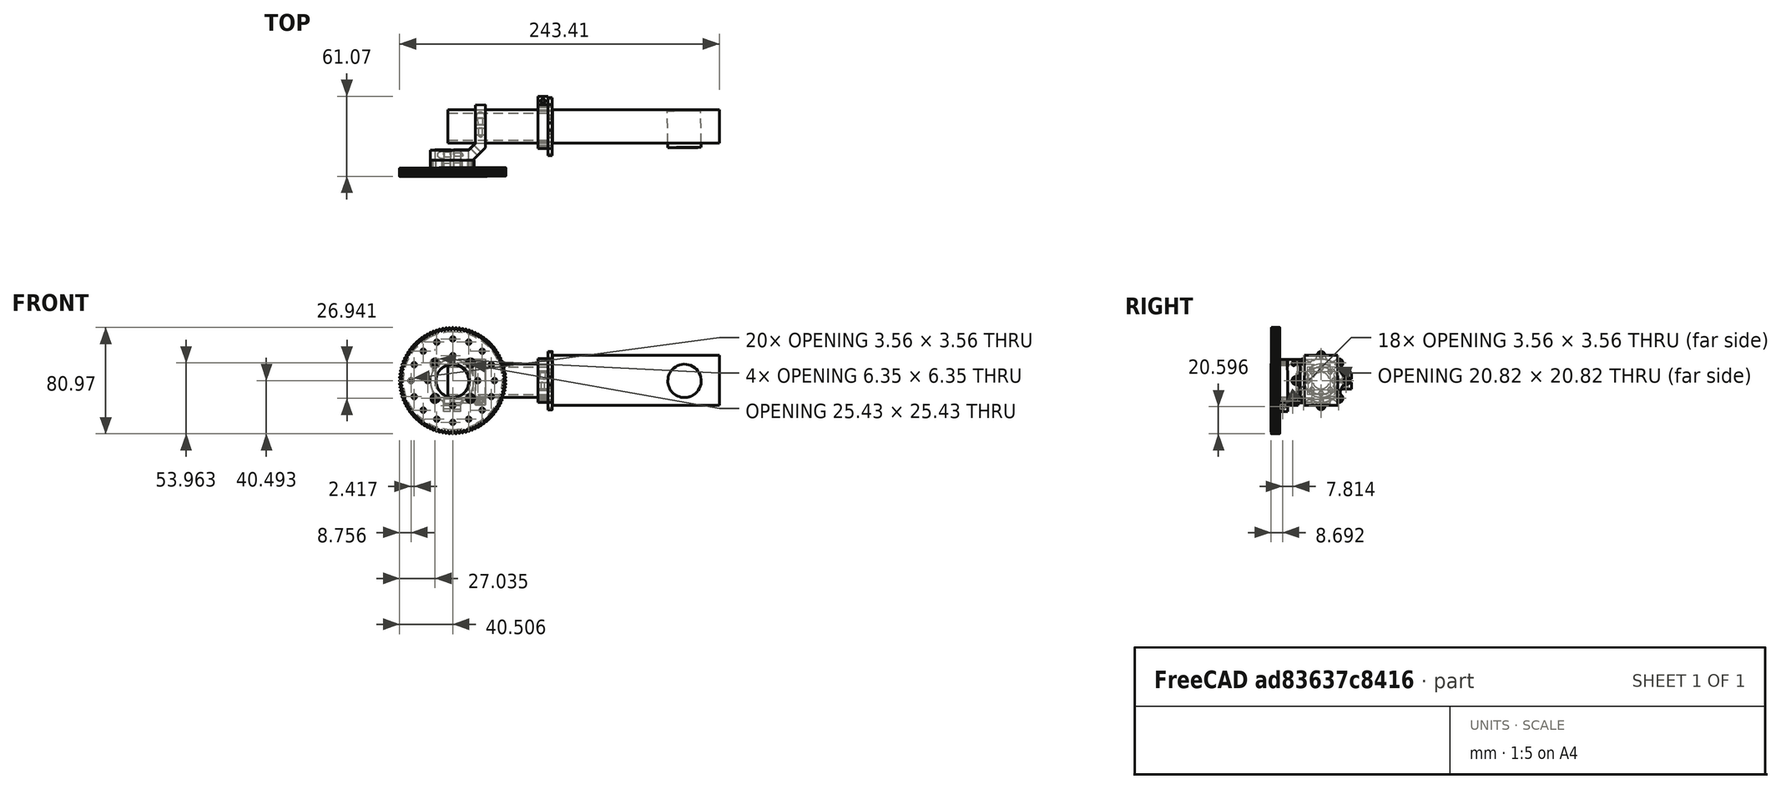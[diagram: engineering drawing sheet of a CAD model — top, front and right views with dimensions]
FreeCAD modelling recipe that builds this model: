
FCSTD DOCUMENT  (FreeCAD 0.15R4671 (Git))
Label: elbow
License: All rights reserved
LicenseURL: http://en.wikipedia.org/wiki/All_rights_reserved
objects: Part::Feature×6, Part::Box×1, Part::Cylinder×1
note: 8 computed .brp shape members not serialized (recipe doc carries the construction recipe); baked Part::Feature solids carry a one-line shape summary decoded from their .brp

FEATURE [Part::Feature] Part__Feature  label="635104"
  Placement = pos=(72.4952,36.2578,0) rot=(0,0,1;1.5708rad)
  shape: bbox 76.2 x 25.39 x 25.39 mm, 6 faces (baked)
FEATURE [Part::Feature] Part__Feature001  label="545354"
  Placement = pos=(72.4952,36.2578,0) rot=(0,0,1;1.5708rad)
  shape: bbox 7.62 x 39.7 x 33.29 mm, 45 faces (baked)
FEATURE [Part::Box] Box  label="Cube"
  Height = 38.1
  Length = 127
  Placement = pos=(75.9089,23.557,-18.7554) rot=(0,0,1;0rad)
  Width = 25.4
FEATURE [Part::Cylinder] Cylinder
  Angle = 360
  Height = 27.94
  Placement = pos=(176.377,20.321,-0.182765) rot=(0.584444,-0.573279,-0.574261;4.18169rad)
  Radius = 12.7
FEATURE [Part::Feature] Part__Feature004  label="545388"
  Placement = pos=(75.6702,36.2578,0) rot=(0,0,1;1.5708rad)
  shape: bbox 3.175 x 44.37 x 44.37 mm, 73 faces (baked)
FEATURE [Part::Feature] Part__Feature005  label="545464"
  Placement = pos=(24.8701,36.2578,-9.63981e-06) rot=(0.579573,-0.579166,0.57329;2.10749rad)
  shape: bbox 41.96 x 42.27 x 35.28 mm, 62 faces (baked)
FEATURE [Part::Feature] Part__Feature006  label="615234"
  Placement = pos=(0,0,0) rot=(-0.000987,-0.000994,-0.999999;1.56718rad)
  shape: bbox 80.99 x 6.684 x 80.98 mm, 898 faces (baked)
FEATURE [Part::Feature] Part__Feature007  label="545352"
  Placement = pos=(-0.492574,3.13161,-0.459087) rot=(0,1,0;1.56789rad)
  shape: bbox 33.37 x 7.62 x 39.76 mm, 45 faces (baked)
